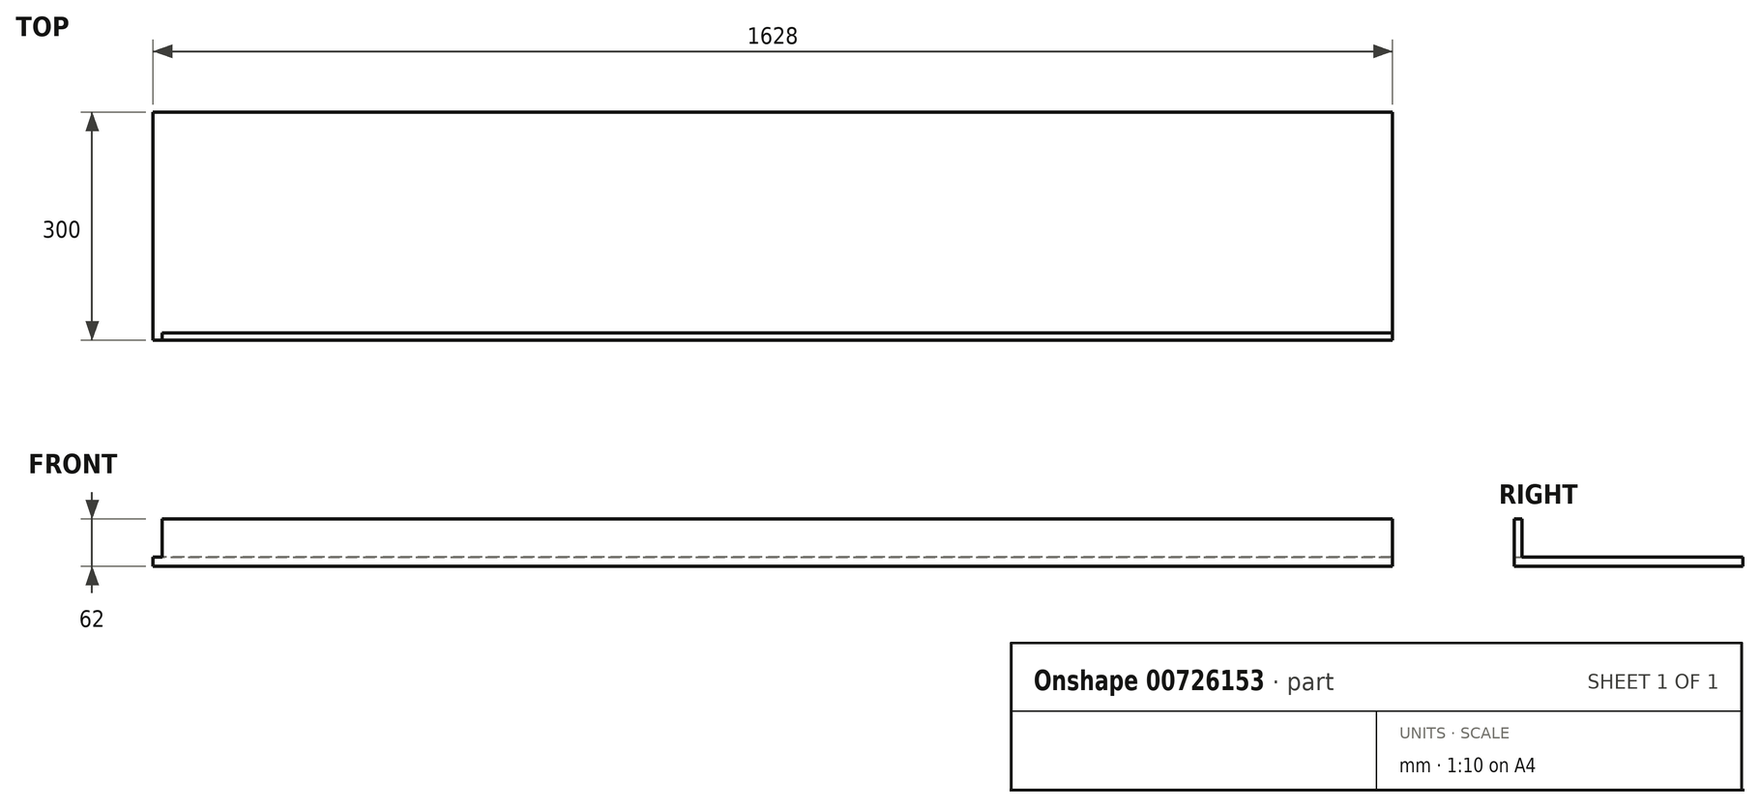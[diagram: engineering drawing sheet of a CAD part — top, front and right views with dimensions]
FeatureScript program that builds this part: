
annotation { "Feature Type Name" : "Feature", "Feature Type Description" : "" }
export const myFeature = defineFeature(function(context is Context, id is Id, definition is map)
    precondition{}
    {
        {
            var Q0;
            Q0=qCreatedBy(makeId("Top.planeOp"),FACE);
            var sketch = newSketch(context, id + "F0", { "sketchPlane" : qUnion([Q0])});
            skLineSegment(sketch, "E0.bottom", {"start": v(-814, 150) * mm, "end": v(814, 150) * mm});
            skLineSegment(sketch, "E0.top", {"start": v(-814, -150) * mm, "end": v(814, -150) * mm});
            skLineSegment(sketch, "E0.left", {"start": v(-814, 150) * mm, "end": v(-814, -150) * mm});
            skLineSegment(sketch, "E0.right", {"start": v(814, 150) * mm, "end": v(814, -150) * mm});
            skLineSegment(sketch, "E1", {"start": v(-814, 0) * mm, "end": v(814, 0) * mm, "construction": true});
            skLineSegment(sketch, "E2", {"start": v(0, -150) * mm, "end": v(0, 150) * mm, "construction": true});
            skSolve(sketch);
        }
        {
            var Q0;
            Q0 = qSketchRegion(id + "F0", true);
            extrude(context, id + "F1", {"entities" : qUnion([Q0]), "depth" : 12 * mm, "offsetDistance" : 25 * mm});
        }
        {
            var Q0;
            Q0=makeQuery(id+"F1.opExtrude","CAP_FACE",FACE,{"disambiguationData":[OSD([sQuery(id+"F0.wireOp",EDGE,"E0.bottom"),sQuery(id+"F0.wireOp",EDGE,"E0.top"),sQuery(id+"F0.wireOp",EDGE,"E0.left"),sQuery(id+"F0.wireOp",EDGE,"E0.right")])],"isStart":false});
            var sketch = newSketch(context, id + "F2", { "sketchPlane" : qUnion([Q0])});
            skLineSegment(sketch, "E3.bottom", {"start": v(814, -150) * mm, "end": v(-802, -150) * mm});
            skLineSegment(sketch, "E3.top", {"start": v(814, -140) * mm, "end": v(-802, -140) * mm});
            skLineSegment(sketch, "E3.left", {"start": v(814, -150) * mm, "end": v(814, -140) * mm});
            skLineSegment(sketch, "E3.right", {"start": v(-802, -150) * mm, "end": v(-802, -140) * mm});
            skSolve(sketch);
        }
        {
            var Q0;
            Q0 = qSketchRegion(id + "F2", true);
            extrude(context, id + "F3", {"entities" : qUnion([Q0]), "operationType" : NewBodyOperationType.ADD, "depth" : 50 * mm, "offsetDistance" : 25 * mm});
        }
    });
